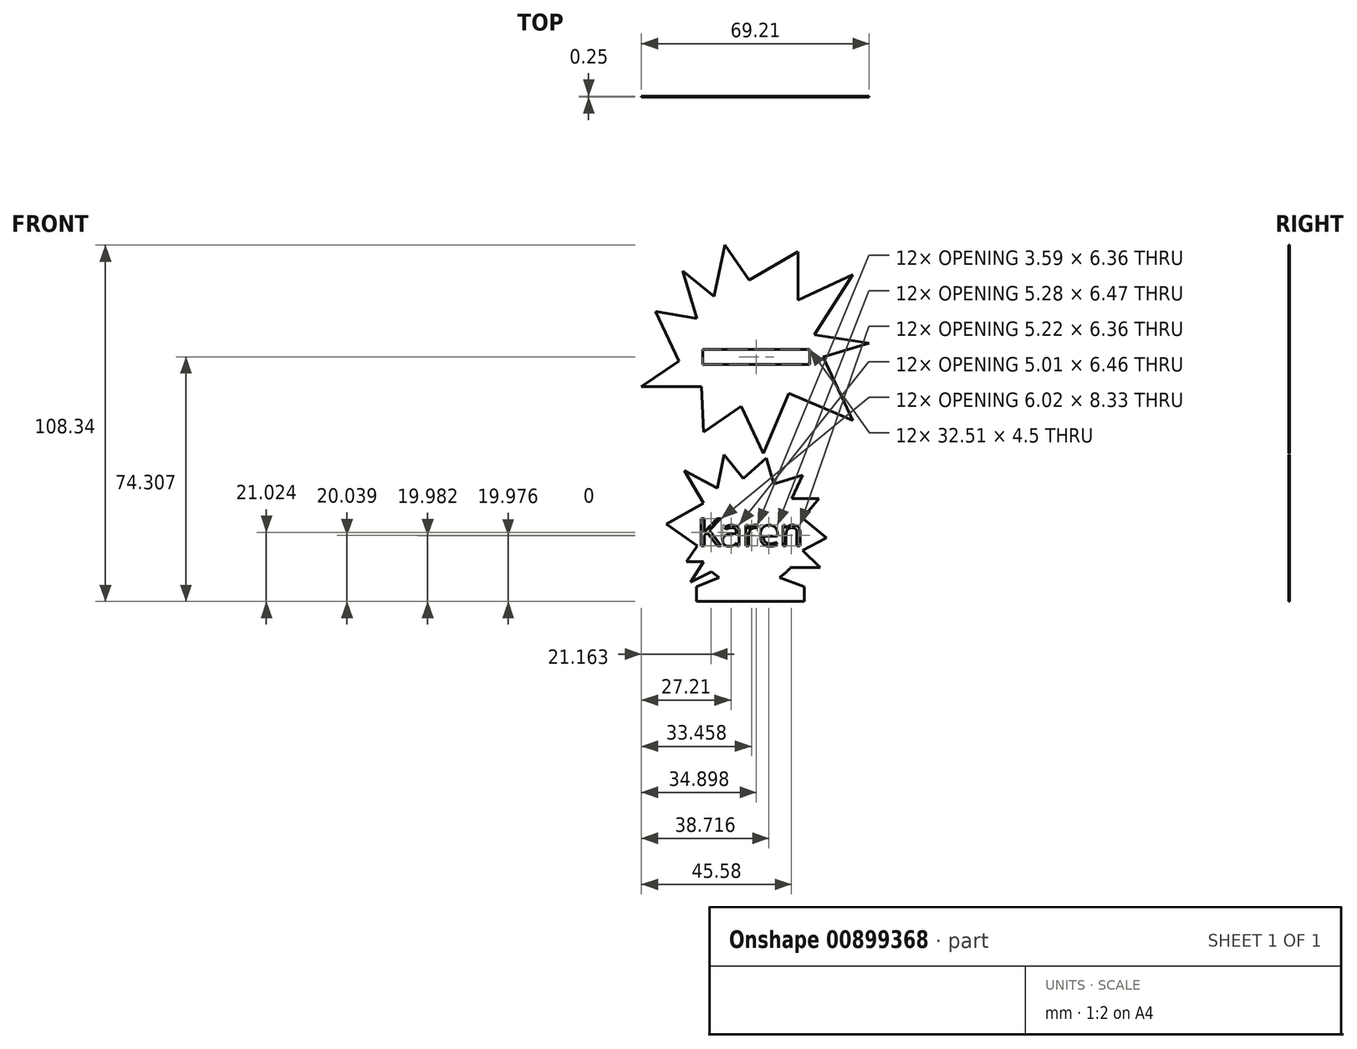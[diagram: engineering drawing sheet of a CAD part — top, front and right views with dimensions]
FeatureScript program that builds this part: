
annotation { "Feature Type Name" : "Feature", "Feature Type Description" : "" }
export const myFeature = defineFeature(function(context is Context, id is Id, definition is map)
    precondition{}
    {
        {
            var Q0;
            Q0=qCreatedBy(makeId("Front.planeOp"),FACE);
            var sketch = newSketch(context, id + "F0", { "sketchPlane" : qUnion([Q0])});
            skLineSegment(sketch, "E0", {"start": v(-7.48, 53.15) * mm, "end": v(7.34, 61.8) * mm});
            skLineSegment(sketch, "E1", {"start": v(7.34, 61.8) * mm, "end": v(7.34, 47.03) * mm});
            skLineSegment(sketch, "E2", {"start": v(7.34, 47.03) * mm, "end": v(23.96, 54.82) * mm});
            skLineSegment(sketch, "E3", {"start": v(23.96, 54.82) * mm, "end": v(12.35, 36.47) * mm});
            skLineSegment(sketch, "E4", {"start": v(12.35, 36.47) * mm, "end": v(28.98, 33.99) * mm});
            skLineSegment(sketch, "E5", {"start": v(28.98, 33.99) * mm, "end": v(14.94, 29.77) * mm});
            skLineSegment(sketch, "E6", {"start": v(14.94, 29.77) * mm, "end": v(23.96, 10.54) * mm});
            skLineSegment(sketch, "E7", {"start": v(4.49, 18.68) * mm, "end": v(23.96, 10.54) * mm});
            skLineSegment(sketch, "E8", {"start": v(4.49, 18.68) * mm, "end": v(-3.14, 0.44) * mm});
            skLineSegment(sketch, "E9", {"start": v(-3.14, 0.44) * mm, "end": v(-9.88, 14.82) * mm});
            skLineSegment(sketch, "E10", {"start": v(-9.88, 14.82) * mm, "end": v(-21.3, 6.98) * mm});
            skLineSegment(sketch, "E11", {"start": v(-21.3, 6.98) * mm, "end": v(-22.02, 20.8) * mm});
            skLineSegment(sketch, "E12", {"start": v(-22.02, 20.8) * mm, "end": v(-40.23, 20.8) * mm});
            skLineSegment(sketch, "E13", {"start": v(-28.89, 28.47) * mm, "end": v(-35.98, 43.6) * mm});
            skLineSegment(sketch, "E14", {"start": v(-35.98, 43.6) * mm, "end": v(-23.35, 41.46) * mm});
            skLineSegment(sketch, "E15", {"start": v(-23.35, 41.46) * mm, "end": v(-27.71, 56) * mm});
            skLineSegment(sketch, "E16", {"start": v(-27.71, 56) * mm, "end": v(-18.17, 48.2) * mm});
            skLineSegment(sketch, "E17", {"start": v(-18.17, 48.2) * mm, "end": v(-14.9, 63.8) * mm});
            skLineSegment(sketch, "E18", {"start": v(-14.9, 63.8) * mm, "end": v(-7.48, 53.15) * mm});
            skLineSegment(sketch, "E19.left", {"start": v(3.35, 18.95) * mm, "end": v(3.35, 18.95) * mm});
            skLineSegment(sketch, "E19.right", {"start": v(8.05, 18.95) * mm, "end": v(8.05, 18.95) * mm});
            skLineSegment(sketch, "E20.bottom", {"start": v(-21.59, 32.02) * mm, "end": v(10.92, 32.02) * mm});
            skLineSegment(sketch, "E20.top", {"start": v(-21.59, 27.52) * mm, "end": v(10.92, 27.52) * mm});
            skLineSegment(sketch, "E20.left", {"start": v(-21.59, 32.02) * mm, "end": v(-21.59, 27.52) * mm});
            skLineSegment(sketch, "E20.right", {"start": v(10.92, 32.02) * mm, "end": v(10.92, 27.52) * mm});
            skArc(sketch, "E21", {"start": v(1.74, -37.22) * mm, "mid": v(3.54, -35.82) * mm, "end": v(5.13, -34.19) * mm});
            skLineSegment(sketch, "E22.top", {"start": v(-23.58, -44.54) * mm, "end": v(9.2, -44.54) * mm});
            skLineSegment(sketch, "E22.left", {"start": v(-23.58, -40.04) * mm, "end": v(-23.58, -44.54) * mm});
            skLineSegment(sketch, "E22.right", {"start": v(9.2, -40.04) * mm, "end": v(9.2, -44.54) * mm});
            skText(sketch, "E23", { "text": "Karen", "fontName": "OpenSans-Regular.ttf"});
            skLineSegment(sketch, "E24", {"start": v(5.13, -34.19) * mm, "end": v(14.11, -34.19) * mm});
            skLineSegment(sketch, "E25", {"start": v(14.11, -34.19) * mm, "end": v(8.74, -28.97) * mm});
            skLineSegment(sketch, "E26", {"start": v(8.74, -28.97) * mm, "end": v(15.97, -25.26) * mm});
            skLineSegment(sketch, "E27", {"start": v(15.97, -25.26) * mm, "end": v(8.74, -19.28) * mm});
            skLineSegment(sketch, "E28", {"start": v(8.74, -19.28) * mm, "end": v(13.73, -13.26) * mm});
            skLineSegment(sketch, "E29", {"start": v(13.73, -13.26) * mm, "end": v(5.44, -13.26) * mm});
            skLineSegment(sketch, "E30", {"start": v(5.44, -13.26) * mm, "end": v(8.74, -6.17) * mm});
            skLineSegment(sketch, "E31", {"start": v(8.74, -6.17) * mm, "end": v(0, -8.81) * mm});
            skLineSegment(sketch, "E32", {"start": v(0, -8.81) * mm, "end": v(-2.37, -0.98) * mm});
            skLineSegment(sketch, "E33", {"start": v(-2.37, -0.98) * mm, "end": v(-9.24, -7.12) * mm});
            skLineSegment(sketch, "E34", {"start": v(-9.24, -7.12) * mm, "end": v(-15.1, 0) * mm});
            skLineSegment(sketch, "E35", {"start": v(-15.1, 0) * mm, "end": v(-17.12, -10.13) * mm});
            skLineSegment(sketch, "E36", {"start": v(-17.12, -10.13) * mm, "end": v(-27.2, -4.74) * mm});
            skLineSegment(sketch, "E37", {"start": v(-27.2, -4.74) * mm, "end": v(-21.37, -14.61) * mm});
            skLineSegment(sketch, "E38", {"start": v(-21.37, -14.61) * mm, "end": v(-32.62, -20.99) * mm});
            skLineSegment(sketch, "E39", {"start": v(-32.62, -20.99) * mm, "end": v(-23.22, -27.68) * mm});
            skLineSegment(sketch, "E40", {"start": v(-23.22, -27.68) * mm, "end": v(-26.61, -32.45) * mm});
            skLineSegment(sketch, "E41", {"start": v(-26.61, -32.45) * mm, "end": v(-21.37, -32.45) * mm});
            skLineSegment(sketch, "E42", {"start": v(-21.37, -32.45) * mm, "end": v(-25.36, -38.66) * mm});
            skLineSegment(sketch, "E43", {"start": v(-25.36, -38.66) * mm, "end": v(-18.9, -35.46) * mm});
            skPoint(sketch, "E44", {"position": v(10.92, 29.77) * mm});
            skLineSegment(sketch, "E45.trimOffspring", {"start": v(-40.23, 20.8) * mm, "end": v(-28.89, 28.47) * mm});
            skLineSegment(sketch, "E46", {"start": v(-18.9, -35.46) * mm, "end": v(-16.71, -37.22) * mm});
            skLineSegment(sketch, "E47", {"start": v(1.74, -37.22) * mm, "end": v(9.2, -40.04) * mm});
            skLineSegment(sketch, "E48", {"start": v(-23.58, -40.04) * mm, "end": v(-16.71, -37.22) * mm});
            const initialGuessF0  = {"E23": [-0.02322, -0.02768, 1, 0, 0.0084]};
            skSetInitialGuess(sketch, initialGuessF0);
            skSolve(sketch);
        }
        {
            var Q0;
            Q0=makeQuery(id+"F0.imprint","IMPRINT",FACE,{"disambiguationData":[TD([[makeQuery(id+"F0.imprint","IMPRINT",EDGE,{"derivedFrom":sQuery(id+"F0.wireOp",EDGE,"E21")}),1.0]])]});
            var Q1;
            Q1=makeQuery(id+"F0.imprint","IMPRINT",FACE,{"disambiguationData":[TD([[makeQuery(id+"F0.imprint","IMPRINT",EDGE,{"derivedFrom":sQuery(id+"F0.wireOp",EDGE,"E0")}),-1.0]])]});
            extrude(context, id + "F1", {"entities" : qUnion([Q0, Q1]), "depth" : .25 * mm, "offsetDistance" : 25 * mm});
        }
    });
